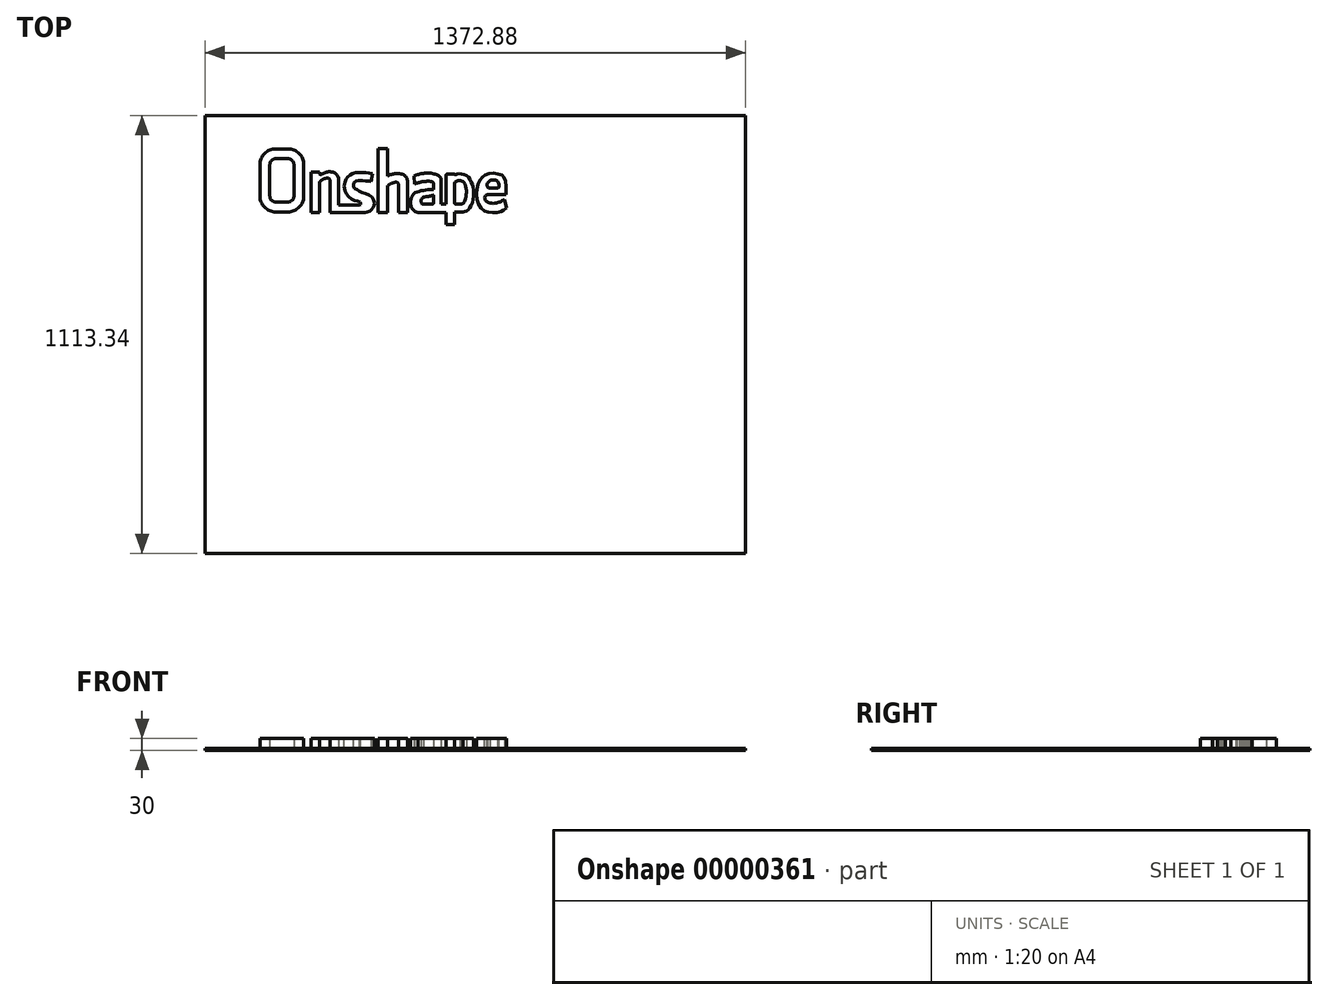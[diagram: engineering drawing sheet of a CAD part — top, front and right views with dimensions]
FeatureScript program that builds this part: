
annotation { "Feature Type Name" : "Feature", "Feature Type Description" : "" }
export const myFeature = defineFeature(function(context is Context, id is Id, definition is map)
    precondition{}
    {
        {
            var Q0;
            Q0 = qCreatedBy(makeId("Top.planeOp"), FACE);
            var sketch = newSketch(context, id + "F0", { "sketchPlane" : qUnion([Q0])});
            skLineSegment(sketch, "E0.bottom", {"start": v(-686.44, 556.67) * mm, "end": v(686.44, 556.67) * mm});
            skLineSegment(sketch, "E0.top", {"start": v(-686.44, -556.67) * mm, "end": v(686.44, -556.67) * mm});
            skLineSegment(sketch, "E0.left", {"start": v(-686.44, 556.67) * mm, "end": v(-686.44, -556.67) * mm});
            skLineSegment(sketch, "E0.right", {"start": v(686.44, 556.67) * mm, "end": v(686.44, -556.67) * mm});
            skLineSegment(sketch, "E1", {"start": v(0, 0) * mm, "end": v(285.59, 0) * mm, "construction": true});
            skLineSegment(sketch, "E2", {"start": v(0, 0) * mm, "end": v(0, 273.23) * mm, "construction": true});
            skPoint(sketch, "E3", {"position": v(686.44, 0) * mm});
            skPoint(sketch, "E4", {"position": v(0, 556.67) * mm});
            skSolve(sketch);
        }
        {
            var Q0;
            Q0=makeQuery(id+"F0.imprint","IMPRINT",FACE,{"disambiguationData":[TD([[makeQuery(id+"F0.imprint","IMPRINT",EDGE,{"derivedFrom":sQuery(id+"F0.wireOp",EDGE,"E0.bottom")}),-1.0]])]});
            extrude(context, id + "F1", {"entities" : qUnion([Q0]), "depth" : 5 * mm});
        }
        {
            var Q0;
            Q0=makeQuery(id+"F1.opExtrude","CAP_FACE",FACE,{"disambiguationData":[OSD([sQuery(id+"F0.wireOp",EDGE,"E0.bottom"),sQuery(id+"F0.wireOp",EDGE,"E0.top"),sQuery(id+"F0.wireOp",EDGE,"E0.left"),sQuery(id+"F0.wireOp",EDGE,"E0.right")])],"isStart":false});
            var sketch = newSketch(context, id + "F2", { "sketchPlane" : qUnion([Q0])});
            skLineSegment(sketch, "E5", {"start": v(-546.86, 431.78) * mm, "end": v(-546.86, 351.63) * mm});
            skLineSegment(sketch, "E6", {"start": v(-506.86, 311.63) * mm, "end": v(-475.63, 311.63) * mm});
            skLineSegment(sketch, "E7", {"start": v(-435.63, 351.63) * mm, "end": v(-435.63, 431.78) * mm});
            skLineSegment(sketch, "E8", {"start": v(-475.63, 471.78) * mm, "end": v(-506.86, 471.78) * mm});
            skPoint(sketch, "E9.visualSharp", {"position": v(-546.86, 311.63) * mm});
            skArc(sketch, "E9.filletArc", {"start": v(-546.86, 351.63) * mm, "mid": v(-535.14, 323.35) * mm, "end": v(-506.86, 311.63) * mm});
            skPoint(sketch, "E10.visualSharp", {"position": v(-435.63, 311.63) * mm});
            skArc(sketch, "E10.filletArc", {"start": v(-475.63, 311.63) * mm, "mid": v(-447.34, 323.35) * mm, "end": v(-435.63, 351.63) * mm});
            skPoint(sketch, "E11.visualSharp", {"position": v(-546.86, 471.78) * mm});
            skArc(sketch, "E11.filletArc", {"start": v(-506.86, 471.78) * mm, "mid": v(-535.14, 460.06) * mm, "end": v(-546.86, 431.78) * mm});
            skPoint(sketch, "E12.visualSharp", {"position": v(-435.63, 471.78) * mm});
            skArc(sketch, "E12.filletArc", {"start": v(-435.63, 431.78) * mm, "mid": v(-447.34, 460.06) * mm, "end": v(-475.63, 471.78) * mm});
            skArc(sketch, "E13.0", {"start": v(-506.86, 446.78) * mm, "mid": v(-517.46, 442.38) * mm, "end": v(-521.86, 431.78) * mm});
            skLineSegment(sketch, "E13.1", {"start": v(-475.63, 446.78) * mm, "end": v(-506.86, 446.78) * mm});
            skArc(sketch, "E13.2", {"start": v(-460.63, 431.78) * mm, "mid": v(-465.02, 442.38) * mm, "end": v(-475.63, 446.78) * mm});
            skLineSegment(sketch, "E13.3", {"start": v(-460.63, 351.63) * mm, "end": v(-460.63, 431.78) * mm});
            skArc(sketch, "E13.4", {"start": v(-475.63, 336.63) * mm, "mid": v(-465.02, 341.03) * mm, "end": v(-460.63, 351.63) * mm});
            skLineSegment(sketch, "E13.5", {"start": v(-521.86, 431.78) * mm, "end": v(-521.86, 351.63) * mm});
            skLineSegment(sketch, "E13.6", {"start": v(-506.86, 336.63) * mm, "end": v(-475.63, 336.63) * mm});
            skArc(sketch, "E13.7", {"start": v(-521.86, 351.63) * mm, "mid": v(-517.46, 341.03) * mm, "end": v(-506.86, 336.63) * mm});
            skLineSegment(sketch, "E14", {"start": v(-417.6, 310.1) * mm, "end": v(-417.6, 412.23) * mm});
            skLineSegment(sketch, "E15", {"start": v(-417.6, 412.23) * mm, "end": v(-395.87, 412.23) * mm});
            skLineSegment(sketch, "E16", {"start": v(-395.87, 412.23) * mm, "end": v(-395.87, 409.6) * mm});
            skLineSegment(sketch, "E17", {"start": v(-395.87, 310.1) * mm, "end": v(-417.6, 310.1) * mm});
            skLineSegment(sketch, "E18", {"start": v(-368.55, 390.13) * mm, "end": v(-368.55, 310.1) * mm});
            skLineSegment(sketch, "E19", {"start": v(-368.55, 310.1) * mm, "end": v(-295.29, 310.1) * mm});
            skLineSegment(sketch, "E20", {"start": v(-295.29, 328.96) * mm, "end": v(-347.44, 328.96) * mm});
            skLineSegment(sketch, "E21", {"start": v(-347.44, 328.96) * mm, "end": v(-347.44, 397.9) * mm});
            skFitSpline(sketch, "E22", {"points": [v(-395.87, 387.32) * mm, v(-385.94, 394.77) * mm, v(-372.9, 397.25) * mm, v(-368.55, 391.05) * mm], "startDerivative": vector(24.47, 22.54) * mm, "endDerivative": vector(10.61, -28.3) * mm});
            skFitSpline(sketch, "E23", {"points": [v(-395.87, 408.63) * mm, v(-393.73, 406.28) * mm, v(-391.12, 406.28) * mm, v(-384.6, 409.93) * mm, v(-374.93, 413.33) * mm, v(-361.62, 412.54) * mm, v(-353.53, 407.85) * mm, v(-347.44, 399.3) * mm], "startDerivative": vector(21.71, -30.96) * mm, "endDerivative": vector(33.67, -55.34) * mm});
            skLineSegment(sketch, "E24.trimOffspring", {"start": v(-395.87, 385.12) * mm, "end": v(-395.87, 310.1) * mm});
            skArc(sketch, "E25.filletArc", {"start": v(-347.44, 397.9) * mm, "mid": v(-347.63, 399.26) * mm, "end": v(-348.18, 400.52) * mm});
            skArc(sketch, "E26.filletArc", {"start": v(-368.55, 390.13) * mm, "mid": v(-368.64, 391.05) * mm, "end": v(-368.89, 391.93) * mm});
            skArc(sketch, "E27.filletArc", {"start": v(-394.22, 388.83) * mm, "mid": v(-395.44, 387.15) * mm, "end": v(-395.87, 385.12) * mm});
            skArc(sketch, "E28.filletArc", {"start": v(-395.87, 409.6) * mm, "mid": v(-395.72, 408.64) * mm, "end": v(-395.27, 407.8) * mm});
            skFitSpline(sketch, "E29", {"points": [v(-295.29, 328.96) * mm, v(-292.05, 329.95) * mm, v(-290.85, 331.9) * mm, v(-292.74, 336.46) * mm, v(-304.79, 340.51) * mm, v(-322.88, 351.7) * mm, v(-331.49, 368.73) * mm, v(-332.62, 378.25) * mm, v(-331.32, 386.02) * mm, v(-325.36, 398.7) * mm, v(-313.45, 408.55) * mm, v(-295.29, 411.92) * mm, v(-273.04, 411.14) * mm, v(-265.01, 409.58) * mm], "startDerivative": vector(84.75, 14.56) * mm, "endDerivative": vector(103.74, -25.5) * mm});
            skLineSegment(sketch, "E30", {"start": v(-295.29, 310.1) * mm, "end": v(-279.88, 310.1) * mm});
            skFitSpline(sketch, "E31", {"points": [v(-279.88, 310.1) * mm, v(-268.3, 312.93) * mm, v(-259.93, 321.25) * mm, v(-256.27, 332.24) * mm, v(-262.13, 348.72) * mm, v(-285.2, 360.44) * mm, v(-301.32, 368.13) * mm, v(-309.02, 374.73) * mm, v(-308.65, 384.25) * mm, v(-301.32, 390.85) * mm, v(-279.88, 390.48) * mm, v(-264.33, 389.01) * mm], "startDerivative": vector(97.21, 0) * mm, "endDerivative": vector(103.18, -17.03) * mm});
            skLineSegment(sketch, "E32", {"start": v(-264.33, 389.01) * mm, "end": v(-261.08, 408.71) * mm});
            skLineSegment(sketch, "E33", {"start": v(-261.08, 408.71) * mm, "end": v(-265.01, 409.58) * mm});
            skLineSegment(sketch, "E34", {"start": v(-247.27, 310.1) * mm, "end": v(-247.27, 472.02) * mm});
            skLineSegment(sketch, "E35", {"start": v(-247.27, 472.02) * mm, "end": v(-222.54, 472.02) * mm});
            skLineSegment(sketch, "E36", {"start": v(-222.54, 472.02) * mm, "end": v(-222.54, 402.9) * mm});
            skLineSegment(sketch, "E37", {"start": v(-222.54, 310.1) * mm, "end": v(-247.27, 310.1) * mm});
            skLineSegment(sketch, "E38", {"start": v(-194.85, 310.1) * mm, "end": v(-194.85, 382.16) * mm});
            skLineSegment(sketch, "E39", {"start": v(-172.25, 384.93) * mm, "end": v(-172.25, 310.1) * mm});
            skLineSegment(sketch, "E40", {"start": v(-172.25, 310.1) * mm, "end": v(-194.85, 310.1) * mm});
            skFitSpline(sketch, "E41", {"points": [v(-222.54, 378) * mm, v(-219.3, 380.68) * mm, v(-212.2, 384.35) * mm, v(-203.9, 386.8) * mm, v(-198.02, 386.55) * mm, v(-195.34, 383.3) * mm, v(-194.85, 380.93) * mm], "startDerivative": vector(19.33, 17.96) * mm, "endDerivative": vector(0, -32.88) * mm});
            skFitSpline(sketch, "E42", {"points": [v(-222.54, 402.9) * mm, v(-218.06, 405.15) * mm, v(-211.14, 407.4) * mm, v(-204.57, 408.95) * mm, v(-194.03, 408.95) * mm, v(-184.7, 407.05) * mm, v(-176.92, 402.2) * mm, v(-172.94, 394.6) * mm, v(-172.25, 387.86) * mm, v(-172.25, 384.93) * mm], "startDerivative": vector(44.62, 25.05) * mm, "endDerivative": vector(-0.44, -37.07) * mm});
            skLineSegment(sketch, "E43.trimOffspring", {"start": v(-222.54, 378) * mm, "end": v(-222.54, 310.1) * mm});
            skFitSpline(sketch, "E44", {"points": [v(-155.69, 402.36) * mm, v(-146.29, 406.3) * mm, v(-137.36, 408.56) * mm, v(-125.69, 410.31) * mm, v(-109.55, 409.3) * mm, v(-98.2, 405.93) * mm, v(-90.64, 401.36) * mm, v(-86.45, 394.88) * mm], "startDerivative": vector(46.04, 27.08) * mm, "endDerivative": vector(2.85, -63.73) * mm});
            skLineSegment(sketch, "E45", {"start": v(-86.45, 394.88) * mm, "end": v(-86.45, 331.29) * mm});
            skLineSegment(sketch, "E46", {"start": v(-145.35, 310.1) * mm, "end": v(-73.7, 310.1) * mm});
            skFitSpline(sketch, "E47", {"points": [v(-145.35, 310.1) * mm, v(-152.18, 312.44) * mm, v(-157.9, 317.24) * mm, v(-163.12, 325.3) * mm, v(-164.18, 338.84) * mm, v(-162.7, 346.6) * mm, v(-157.3, 356.7) * mm, v(-146.8, 362.57) * mm, v(-132.2, 366.32) * mm, v(-117.08, 367.97) * mm, v(-105.47, 368.73) * mm], "startDerivative": vector(-83.06, 22.5) * mm, "endDerivative": vector(90.2, 15.78) * mm});
            skLineSegment(sketch, "E48", {"start": v(-105.47, 368.73) * mm, "end": v(-105.47, 381.7) * mm});
            skLineSegment(sketch, "E49", {"start": v(-155.69, 402.36) * mm, "end": v(-154.02, 382.77) * mm});
            skFitSpline(sketch, "E50", {"points": [v(-154.02, 382.77) * mm, v(-144.61, 385.73) * mm, v(-136.68, 387.76) * mm, v(-127.98, 389.02) * mm, v(-120.42, 389.61) * mm, v(-113.87, 389.11) * mm, v(-108.78, 387.18) * mm, v(-105.47, 381.7) * mm], "startDerivative": vector(58.12, 18.51) * mm, "endDerivative": vector(-2.77, -59.3) * mm});
            skLineSegment(sketch, "E51", {"start": v(-105.47, 353.65) * mm, "end": v(-105.47, 336.09) * mm});
            skLineSegment(sketch, "E52", {"start": v(-130.8, 331.09) * mm, "end": v(-110.47, 331.09) * mm});
            skFitSpline(sketch, "E53", {"points": [v(-130.8, 331.09) * mm, v(-134.75, 332.12) * mm, v(-136.48, 334.09) * mm, v(-137.47, 338.28) * mm, v(-136.48, 343.8) * mm, v(-132.78, 348.23) * mm, v(-124.06, 350.62) * mm, v(-114.28, 351.69) * mm, v(-110.25, 352.84) * mm, v(-107.99, 353.65) * mm, v(-106.71, 354.4) * mm, v(-105.85, 354.11) * mm, v(-105.47, 353.65) * mm], "startDerivative": vector(-49.56, 8.3) * mm, "endDerivative": vector(5.14, -15.4) * mm});
            skArc(sketch, "E54.filletArc", {"start": v(-110.47, 331.09) * mm, "mid": v(-106.94, 332.55) * mm, "end": v(-105.47, 336.09) * mm});
            skLineSegment(sketch, "E55", {"start": v(-86.45, 331.29) * mm, "end": v(-73.7, 331.29) * mm});
            skLineSegment(sketch, "E56", {"start": v(-73.7, 331.29) * mm, "end": v(-73.7, 405.67) * mm});
            skLineSegment(sketch, "E57", {"start": v(-73.7, 310.1) * mm, "end": v(-73.7, 279.1) * mm});
            skLineSegment(sketch, "E58", {"start": v(-73.7, 279.1) * mm, "end": v(-52.5, 279.1) * mm});
            skLineSegment(sketch, "E59", {"start": v(-52.5, 279.1) * mm, "end": v(-52.5, 311) * mm});
            skLineSegment(sketch, "E60", {"start": v(-52.5, 311) * mm, "end": v(-31.56, 311) * mm});
            skLineSegment(sketch, "E61", {"start": v(-52.5, 334.29) * mm, "end": v(-52.5, 385.08) * mm});
            skLineSegment(sketch, "E62", {"start": v(-71.7, 407.67) * mm, "end": v(-52.5, 407.67) * mm});
            skArc(sketch, "E63.filletArc", {"start": v(-71.7, 407.67) * mm, "mid": v(-73.12, 407.09) * mm, "end": v(-73.7, 405.67) * mm});
            skLineSegment(sketch, "E64", {"start": v(-49.5, 331.29) * mm, "end": v(-38.01, 331.29) * mm});
            skPoint(sketch, "E65.newPointA", {"position": v(-52.5, 331.29) * mm});
            skArc(sketch, "E65.filletArc", {"start": v(-52.5, 334.29) * mm, "mid": v(-51.62, 332.17) * mm, "end": v(-49.5, 331.29) * mm});
            skFitSpline(sketch, "E66", {"points": [v(-52.5, 385.08) * mm, v(-49.94, 388.2) * mm, v(-47.38, 389.83) * mm, v(-43.9, 391.23) * mm, v(-38.77, 391.46) * mm, v(-32.5, 389.37) * mm, v(-26.91, 383.09) * mm, v(-22.96, 368.9) * mm, v(-22.96, 354.02) * mm, v(-24.82, 343.32) * mm, v(-29.24, 334.94) * mm, v(-33.66, 332.15) * mm, v(-38.01, 331.29) * mm], "startDerivative": vector(39.46, 54.88) * mm, "endDerivative": vector(-66.44, -9.1) * mm});
            skFitSpline(sketch, "E67", {"points": [v(-52.5, 407.67) * mm, v(-52.5, 406.79) * mm, v(-51.95, 406) * mm, v(-49.85, 406.37) * mm, v(-47.08, 407.67) * mm, v(-42.4, 408.34) * mm, v(-31.43, 407.67) * mm, v(-20.88, 402.7) * mm, v(-14.3, 395.36) * mm, v(-8.1, 383.03) * mm, v(-4.79, 370.91) * mm, v(-3.97, 354.44) * mm, v(-6.97, 335.74) * mm, v(-13.61, 322.35) * mm, v(-20.42, 315.24) * mm, v(-25.52, 312.77) * mm, v(-31.56, 311) * mm], "startDerivative": vector(-4.32, -40.56) * mm, "endDerivative": vector(-113.2, -25.5) * mm});
            skPoint(sketch, "E68.orphan", {"position": v(-86.45, 395.44) * mm});
            skFitSpline(sketch, "E69", {"points": [v(79.8, 321.72) * mm, v(72.86, 316.47) * mm, v(68.09, 313.95) * mm, v(61.94, 311.74) * mm, v(52.56, 310) * mm, v(38.01, 309.82) * mm, v(29.22, 311.62) * mm, v(21.33, 315.8) * mm, v(12.16, 323.85) * mm, v(6.23, 336.9) * mm, v(3.46, 351.75) * mm, v(3.78, 368.7) * mm, v(7.04, 382.57) * mm, v(12.79, 393.95) * mm, v(18.22, 399.99) * mm, v(23.27, 404.6) * mm, v(31.61, 408.55) * mm, v(43.68, 410.09) * mm, v(56.42, 408.77) * mm, v(66.3, 405.7) * mm, v(71.56, 401.74) * mm, v(75.51, 394.5) * mm, v(77.49, 386.38) * mm, v(77.7, 356.3) * mm], "startDerivative": vector(-94.33, -93.91) * mm, "endDerivative": vector(-10.07, -512.06) * mm});
            skLineSegment(sketch, "E70", {"start": v(77.7, 356.3) * mm, "end": v(30.73, 356.3) * mm});
            skFitSpline(sketch, "E71", {"points": [v(30.73, 356.3) * mm, v(26.12, 352.57) * mm, v(24.16, 347.8) * mm, v(24.56, 344.05) * mm, v(26.23, 340.56) * mm, v(29.2, 337.79) * mm, v(34.2, 335.06) * mm, v(43.39, 333.35) * mm, v(55.3, 334.72) * mm, v(61.2, 336.58) * mm, v(68.12, 339.58) * mm, v(74.13, 342.72) * mm], "startDerivative": vector(-38.92, -19.1) * mm, "endDerivative": vector(57.68, 31.07) * mm});
            skLineSegment(sketch, "E72", {"start": v(74.13, 342.72) * mm, "end": v(79.8, 321.72) * mm});
            skLineSegment(sketch, "E73", {"start": v(37.23, 371.87) * mm, "end": v(56.14, 371.87) * mm});
            skFitSpline(sketch, "E74", {"points": [v(56.14, 371.87) * mm, v(58.04, 372.46) * mm, v(59.7, 374.29) * mm, v(60, 377.9) * mm, v(59.65, 382.65) * mm, v(57.56, 388.11) * mm, v(53.95, 391.6) * mm, v(47.9, 392.88) * mm, v(40.58, 392.18) * mm, v(35.58, 389.16) * mm, v(32.45, 386.12) * mm, v(30.54, 381.4) * mm, v(30.86, 376.06) * mm, v(33.07, 373.46) * mm, v(37.23, 371.87) * mm], "startDerivative": vector(39.67, 11.95) * mm, "endDerivative": vector(102.32, -7.72) * mm});
            skSolve(sketch);
        }
        {
            var Q0;
            {Q0=qUnion([makeQuery(id+"F2.imprint","IMPRINT",FACE,{"disambiguationData":[TD([[makeQuery(id+"F2.imprint","IMPRINT",EDGE,{"derivedFrom":sQuery(id+"F2.wireOp",EDGE,"E14")}),-1.0]])]}),makeQuery(id+"F2.imprint","IMPRINT",FACE,{"disambiguationData":[TD([[makeQuery(id+"F2.imprint","IMPRINT",EDGE,{"derivedFrom":sQuery(id+"F2.wireOp",EDGE,"E34")}),-1.0]])]}),makeQuery(id+"F2.imprint","IMPRINT",FACE,{"disambiguationData":[TD([[makeQuery(id+"F2.imprint","IMPRINT",EDGE,{"derivedFrom":sQuery(id+"F2.wireOp",EDGE,"E5")}),1.0]])]}),makeQuery(id+"F2.imprint","IMPRINT",FACE,{"disambiguationData":[TD([[makeQuery(id+"F2.imprint","IMPRINT",EDGE,{"derivedFrom":sQuery(id+"F2.wireOp",EDGE,"E69")}),-1.0]])]}),makeQuery(id+"F2.imprint","IMPRINT",FACE,{"disambiguationData":[TD([[makeQuery(id+"F2.imprint","IMPRINT",EDGE,{"derivedFrom":sQuery(id+"F2.wireOp",EDGE,"E44")}),-1.0]])]})]);}
            extrude(context, id + "F3", {"entities" : qUnion([Q0]), "operationType" : NewBodyOperationType.ADD, "depth" : 25 * mm});
        }
    });
